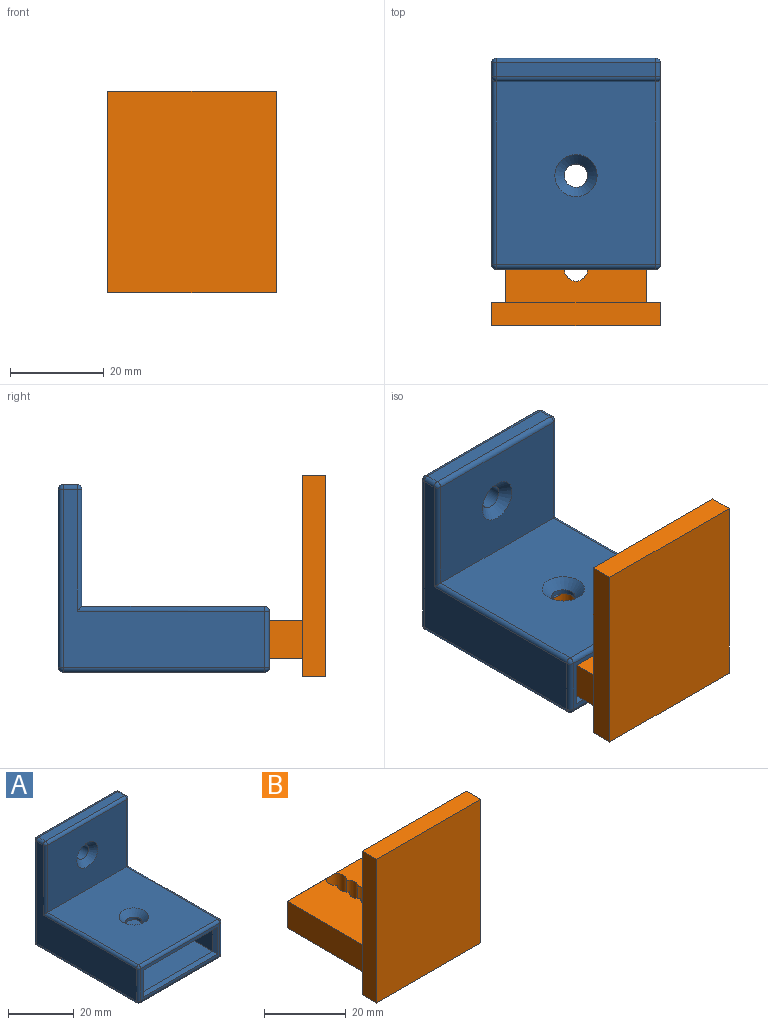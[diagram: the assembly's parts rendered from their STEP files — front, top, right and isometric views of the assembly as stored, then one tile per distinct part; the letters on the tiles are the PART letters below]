
ASSEMBLY  parts=2 mates=1
PART A: 49 faces, bbox 36x45x40 mm
  f0: plane 39x30mm, normal (0,0,-1), area 1150.4mm2, adj f1,f7,f10,f12,f46
  f1: plane 39x8mm, normal (-1,0,0), area 312mm2, adj f0,f2,f12,f48
  f2: plane 39x30mm, normal (0,0,1), area 1150.4mm2, adj f1,f7,f9,f12,f47
  f3: plane 43x38mm, normal (1,0,0), area 594mm2, adj f18,f20,f24,f25,f30,f31
  f4: plane 39x34mm, normal (0,0,1), area 1262.4mm2, adj f11,f13,f24,f36,f42
  f5: plane 43x38mm, normal (-1,0,0), area 594mm2, adj f27,f28,f37,f38,f42,f43
  f6: plane 43x34mm, normal (0,0,-1), area 1442.4mm2, adj f9,f18,f19,f26,f27
  f7: plane 39x8mm, normal (1,0,0), area 312mm2, adj f0,f2,f12,f45
  f8: plane 34x12mm, normal (0,-1,0), area 88mm2, adj f25,f26,f36,f37,f45,f46,f47,f48
  f9: cylinder r=2.5mm len=5mm, axis (0,0,1), area 47.1mm2, adj f2,f6
  f10: cylinder r=2.5mm len=5mm, axis (0,0,1), area 15.7mm2, adj f0,f11
  f11: cone r=2.5mm half-angle=45deg, axis (0,0,1), area 62.2mm2, adj f4,f10
  f12: plane 30x8mm, normal (0,-1,0), area 240mm2, adj f0,f1,f2,f7
  f13: plane 34x25mm, normal (0,-1,0), area 786.4mm2, adj f4,f31,f39,f43,f44
  f14: plane 38x34mm, normal (0,1,0), area 1272.4mm2, adj f16,f19,f20,f28,f29
  f15: plane 34x3mm, normal (0,0,1), area 102mm2, adj f29,f30,f38,f39
  f16: cylinder r=2.5mm len=5mm, axis (0,-1,0), area 47.1mm2, adj f14,f44
  f17: sphere r=1mm, area 1.6mm2, adj f18,f19,f20
  f18: cylinder r=1mm len=43mm, axis (0,-1,0), area 67.5mm2, adj f3,f6,f17,f21
  f19: cylinder r=1mm len=34mm, axis (-1,0,0), area 53.4mm2, adj f6,f14,f17,f22
  f20: cylinder r=1mm len=38mm, axis (0,0,1), area 59.7mm2, adj f3,f14,f17,f23
  f21: sphere r=1mm, area 1.6mm2, adj f18,f25,f26
  f22: sphere r=1mm, area 1.6mm2, adj f19,f27,f28
  f23: sphere r=1mm, area 1.6mm2, adj f20,f29,f30
  f24: cylinder r=1mm len=40mm, axis (0,1,0), area 61.8mm2, adj f3,f4,f31,f32
  f25: cylinder r=1mm len=12mm, axis (0,0,1), area 18.8mm2, adj f3,f8,f21,f32
  f26: cylinder r=1mm len=34mm, axis (1,0,0), area 53.4mm2, adj f6,f8,f21,f33
  f27: cylinder r=1mm len=43mm, axis (0,1,0), area 67.5mm2, adj f5,f6,f22,f33
  f28: cylinder r=1mm len=38mm, axis (0,0,-1), area 59.7mm2, adj f5,f14,f22,f34
  f29: cylinder r=1mm len=34mm, axis (-1,0,0), area 53.4mm2, adj f14,f15,f23,f34
  f30: cylinder r=1mm len=3mm, axis (0,1,0), area 4.7mm2, adj f3,f15,f23,f35
  f31: cylinder r=1mm len=26mm, axis (0,0,1), area 39.8mm2, adj f3,f13,f24,f35
  f32: sphere r=1mm, area 1.6mm2, adj f24,f25,f36
  f33: sphere r=1mm, area 1.6mm2, adj f26,f27,f37
  f34: sphere r=1mm, area 1.6mm2, adj f28,f29,f38
  f35: sphere r=1mm, area 1.6mm2, adj f30,f31,f39
  f36: cylinder r=1mm len=34mm, axis (-1,0,0), area 53.4mm2, adj f4,f8,f32,f40
  f37: cylinder r=1mm len=12mm, axis (0,0,-1), area 18.8mm2, adj f5,f8,f33,f40
  f38: cylinder r=1mm len=3mm, axis (0,-1,0), area 4.7mm2, adj f5,f15,f34,f41
  f39: cylinder r=1mm len=34mm, axis (1,0,0), area 53.4mm2, adj f13,f15,f35,f41
  f40: sphere r=1mm, area 1.6mm2, adj f36,f37,f42
  f41: sphere r=1mm, area 1.6mm2, adj f38,f39,f43
  f42: cylinder r=1mm len=40mm, axis (0,-1,0), area 61.8mm2, adj f4,f5,f40,f43
  f43: cylinder r=1mm len=26mm, axis (0,0,-1), area 39.8mm2, adj f5,f13,f41,f42
  f44: cone r=2.5mm half-angle=45deg, axis (0,-1,0), area 62.2mm2, adj f13,f16
  f45: plane 10x1mm, normal (0.71,-0.71,0), area 12.7mm2, adj f7,f8,f46,f47
  f46: plane 32x1mm, normal (0,-0.71,-0.71), area 43.8mm2, adj f0,f8,f45,f48
  f47: plane 32x1mm, normal (0,-0.71,0.71), area 43.8mm2, adj f2,f8,f45,f48
  f48: plane 10x1mm, normal (-0.71,-0.71,0), area 12.7mm2, adj f1,f8,f46,f47
PART B: 25 faces, bbox 36x35x43 mm
  f0: plane 29x8mm, normal (1,0,0), area 232mm2, adj f2,f3,f5,f16
  f1: plane 29x8mm, normal (-1,0,0), area 232mm2, adj f2,f3,f5,f19
  f2: plane 30x29mm, normal (0,0,-1), area 763.4mm2, adj f0,f1,f5,f6,f7,f8,f9,f10
  f3: plane 30x29mm, normal (0,0,1), area 763.4mm2, adj f0,f1,f5,f6,f7,f8,f9,f10
  f4: plane 28x6mm, normal (0,1,0), area 168mm2, adj f16,f17,f18,f19
  f5: plane 43x36mm, normal (0,1,0), area 1308mm2, adj f0,f1,f2,f3,f20,f21,f22,f23
  f6: cylinder r=2.5mm len=8mm, axis (0,0,1), area 97.8mm2, adj f2,f3,f7,f15,f17,f18
  f7: cylinder r=2.5mm len=8mm, axis (0,0,1), area 37.1mm2, adj f2,f3,f6,f8
  f8: cylinder r=2.5mm len=8mm, axis (0,0,1), area 37.1mm2, adj f2,f3,f7,f9
  f9: cylinder r=2.5mm len=8mm, axis (0,0,1), area 37.1mm2, adj f2,f3,f8,f10
  f10: cylinder r=2.5mm len=8mm, axis (0,0,1), area 37.1mm2, adj f2,f3,f9,f11
  f11: cylinder r=2.5mm len=8mm, axis (0,0,1), area 99.9mm2, adj f2,f3,f10,f12
  f12: cylinder r=2.5mm len=8mm, axis (0,0,1), area 37.1mm2, adj f2,f3,f11,f13
  f13: cylinder r=2.5mm len=8mm, axis (0,0,1), area 37.1mm2, adj f2,f3,f12,f14
  f14: cylinder r=2.5mm len=8mm, axis (0,0,1), area 37.1mm2, adj f2,f3,f13,f15
  f15: cylinder r=2.5mm len=8mm, axis (0,0,1), area 37.1mm2, adj f2,f3,f6,f14
  f16: plane 8x1mm, normal (0.71,0.71,0), area 9.9mm2, adj f0,f4,f17,f18
  f17: plane 30x1mm, normal (0,0.71,0.71), area 39.6mm2, adj f3,f4,f6,f16,f19
  f18: plane 30x1mm, normal (0,0.71,-0.71), area 39.6mm2, adj f2,f4,f6,f16,f19
  f19: plane 8x1mm, normal (-0.71,0.71,0), area 9.9mm2, adj f1,f4,f17,f18
  f20: plane 43x5mm, normal (1,0,0), area 215mm2, adj f5,f21,f23,f24
  f21: plane 36x5mm, normal (0,0,1), area 180mm2, adj f5,f20,f22,f24
  f22: plane 43x5mm, normal (-1,0,0), area 215mm2, adj f5,f21,f23,f24
  f23: plane 36x5mm, normal (0,0,-1), area 180mm2, adj f5,f20,f22,f24
  f24: plane 43x36mm, normal (0,-1,0), area 1548mm2, adj f20,f21,f22,f23
PLACE A t=(2.92,-4.61,9.51)mm
PLACE B t=(2.92,-11.63,9.51)mm
MATE planar B.f2 <-> A.f2  axis (0,0,-1) through (17.92,2.87,5.51)mm
